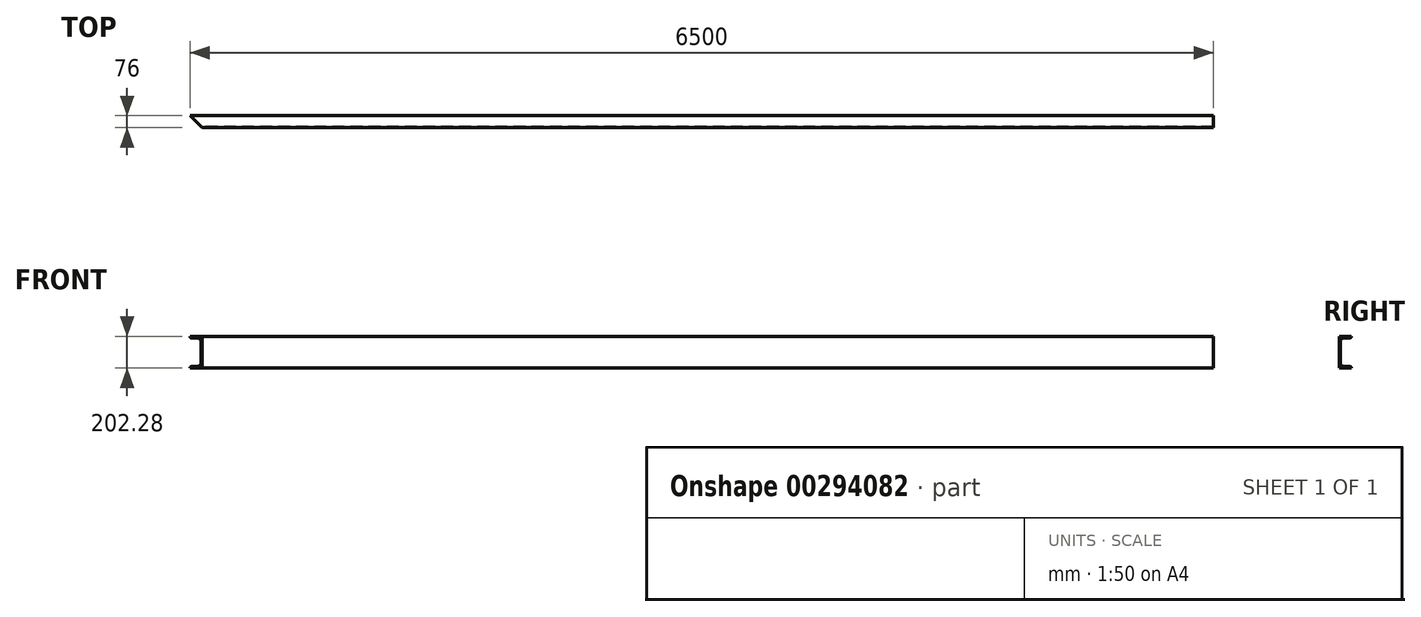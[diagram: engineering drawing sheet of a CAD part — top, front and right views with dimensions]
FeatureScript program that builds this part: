
annotation { "Feature Type Name" : "Feature", "Feature Type Description" : "" }
export const myFeature = defineFeature(function(context is Context, id is Id, definition is map)
    precondition{}
    {
        {
            var Q0;
            Q0=qCreatedBy(makeId("Right.planeOp"),FACE);
            var sketch = newSketch(context, id + "F0", { "sketchPlane" : qUnion([Q0])});
            skLineSegment(sketch, "E0", {"start": v(0, 0) * mm, "end": v(0, 203) * mm});
            skLineSegment(sketch, "E1", {"start": v(0, 203) * mm, "end": v(76, 203) * mm});
            skLineSegment(sketch, "E2", {"start": v(76, 203) * mm, "end": v(76, 201.67) * mm});
            skLineSegment(sketch, "E3", {"start": v(7.1, 173.86) * mm, "end": v(7.1, 29.86) * mm});
            skLineSegment(sketch, "E4", {"start": v(41.55, 191.8) * mm, "end": v(41.55, 278.39) * mm, "construction": true});
            skLineSegment(sketch, "E5", {"start": v(23.21, 190.84) * mm, "end": v(67.94, 193.18) * mm});
            skPoint(sketch, "E6.orphan", {"position": v(76, 193.47) * mm});
            skPoint(sketch, "E7.visualSharp", {"position": v(7.1, 190) * mm});
            skArc(sketch, "E7.filletArc", {"start": v(23.21, 190.84) * mm, "mid": v(11.77, 185.56) * mm, "end": v(7.1, 173.86) * mm});
            skPoint(sketch, "E8.visualSharp", {"position": v(76, 193.6) * mm});
            skArc(sketch, "E8.filletArc", {"start": v(67.94, 193.18) * mm, "mid": v(73.67, 195.82) * mm, "end": v(76, 201.67) * mm});
            skLineSegment(sketch, "E9", {"start": v(7.1, 101.86) * mm, "end": v(142.57, 101.86) * mm, "construction": true});
            skLineSegment(sketch, "E10.MirrorCS", {"start": v(76, 0.72) * mm, "end": v(76, 2.05) * mm});
            skArc(sketch, "E11.MirrorCS", {"start": v(67.94, 10.54) * mm, "mid": v(73.67, 7.9) * mm, "end": v(76, 2.05) * mm});
            skLineSegment(sketch, "E12.MirrorCS", {"start": v(23.21, 12.89) * mm, "end": v(67.94, 10.54) * mm});
            skLineSegment(sketch, "E13.MirrorCS", {"start": v(0, 0.72) * mm, "end": v(76, 0.72) * mm});
            skPoint(sketch, "E14.MirrorP", {"position": v(76, 10.12) * mm});
            skPoint(sketch, "E15.MirrorP", {"position": v(7.1, 13.73) * mm});
            skArc(sketch, "E16.MirrorCS", {"start": v(23.21, 12.89) * mm, "mid": v(11.77, 18.16) * mm, "end": v(7.1, 29.86) * mm});
            skPoint(sketch, "E17.MirrorP", {"position": v(76, 10.26) * mm});
            skSolve(sketch);
        }
        {
            var Q0;
            Q0 = qSketchRegion(id + "F0", true);
            extrude(context, id + "F1", {"entities" : qUnion([Q0]), "depth" : 6500 * mm});
        }
        {
            var Q0;
            Q0=qCreatedBy(makeId("Top.planeOp"),FACE);
            var sketch = newSketch(context, id + "F2", { "sketchPlane" : qUnion([Q0])});
            skLineSegment(sketch, "E18.bottom", {"start": v(0, 0) * mm, "end": v(76, 0) * mm});
            skLineSegment(sketch, "E18.left", {"start": v(0, 0) * mm, "end": v(0, 76) * mm});
            skLineSegment(sketch, "E19", {"start": v(0, 76) * mm, "end": v(76, 0) * mm});
            skSolve(sketch);
        }
        {
            var Q0;
            Q0 = qSketchRegion(id + "F2", true);
            extrude(context, id + "F3", {"entities" : qUnion([Q0]), "operationType" : NewBodyOperationType.REMOVE, "endBound" : BoundingType.THROUGH_ALL, "depth" : 25 * mm});
        }
        {
            var Q0;
            Q0=qCreatedBy(makeId("Right.planeOp"),FACE);
            cPlane(context, id + "F4", {"entities" : qUnion([Q0]), "cplaneType" : CPlaneType.OFFSET, "offset" : (6500 / 2) * mm, "width" : 150 * mm, "height" : 150 * mm});
        }
    });
